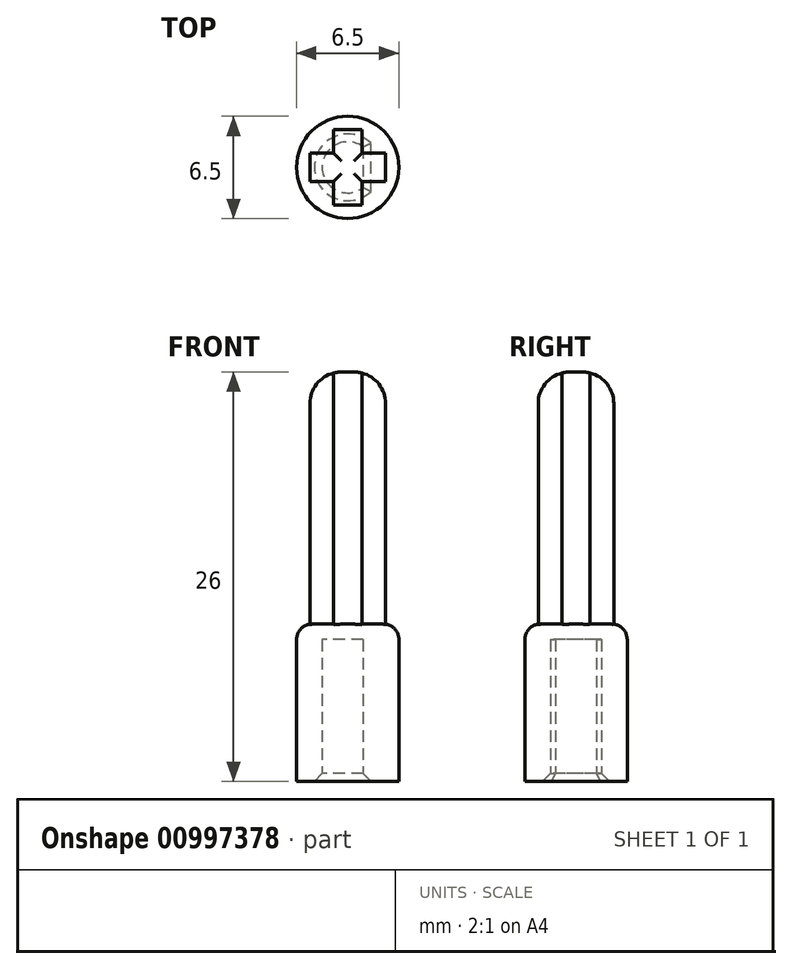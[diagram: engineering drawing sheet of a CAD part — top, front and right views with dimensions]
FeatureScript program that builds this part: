
annotation { "Feature Type Name" : "Feature", "Feature Type Description" : "" }
export const myFeature = defineFeature(function(context is Context, id is Id, definition is map)
    precondition{}
    {
        {
            var Q0;
            Q0=qCreatedBy(makeId("Top.planeOp"),FACE);
            var sketch = newSketch(context, id + "F0", { "sketchPlane" : qUnion([Q0])});
            skCircle(sketch, "E0", {"center": v(0, 0) * mm, "radius": 3.25 * mm});
            skCircle(sketch, "E1", {"center": v(0, 0) * mm, "radius": 1.63 * mm});
            skLineSegment(sketch, "E2", {"start": v(0.98, 1.3) * mm, "end": v(0.98, -1.3) * mm});
            skSolve(sketch);
        }
        {
            var Q0;
            Q0=makeQuery(id+"F0.imprint","IMPRINT",FACE,{"disambiguationData":[TD([[makeQuery(id+"F0.imprint","IMPRINT",EDGE,{"derivedFrom":sQuery(id+"F0.wireOp",EDGE,"E0")}),1.0]])]});
            var Q1;
            {var subQ0=sQuery(id+"F0.wireOp",EDGE,"E2");Q1=makeQuery(id+"F0.imprint","IMPRINT",FACE,{"disambiguationData":[TD([[makeQuery(id+"F0.imprint","IMPRINT",EDGE,{"derivedFrom":subQ0}),1.0]])]});}
            extrude(context, id + "F1", {"entities" : qUnion([Q0, Q1]), "depth" : 9 * mm, "offsetDistance" : 25 * mm});
        }
        {
            var Q0;
            Q0=makeQuery(id+"F1.opExtrude","CAP_FACE",FACE,{"disambiguationData":[OSD([sQuery(id+"F0.wireOp",EDGE,"E0"),sQuery(id+"F0.wireOp",EDGE,"E1"),sQuery(id+"F0.wireOp",EDGE,"E2")])],"isStart":false});
            var sketch = newSketch(context, id + "F2", { "sketchPlane" : qUnion([Q0])});
            skCircle(sketch, "E3", {"center": v(0, 0) * mm, "radius": 3.25 * mm});
            skSolve(sketch);
        }
        {
            var Q0;
            Q0 = qSketchRegion(id + "F2", true);
            extrude(context, id + "F3", {"entities" : qUnion([Q0]), "operationType" : NewBodyOperationType.ADD, "depth" : 1 * mm, "offsetDistance" : 25 * mm});
        }
        {
            var Q0;
            Q0=makeQuery(id+"F3.opExtrude","CAP_FACE",FACE,{"disambiguationData":[OSD([sQuery(id+"F2.wireOp",EDGE,"E3")])],"isStart":false});
            var sketch = newSketch(context, id + "F4", { "sketchPlane" : qUnion([Q0])});
            skLineSegment(sketch, "E4", {"start": v(-2.4, 0.9) * mm, "end": v(-2.4, -0.9) * mm});
            skLineSegment(sketch, "E5", {"start": v(-2.4, -0.9) * mm, "end": v(-0.9, -0.9) * mm});
            skLineSegment(sketch, "E6", {"start": v(-0.9, -0.9) * mm, "end": v(-0.9, -2.4) * mm});
            skLineSegment(sketch, "E7", {"start": v(-0.9, -2.4) * mm, "end": v(0.9, -2.4) * mm});
            skLineSegment(sketch, "E8", {"start": v(0.9, -2.4) * mm, "end": v(0.9, -0.9) * mm});
            skLineSegment(sketch, "E9", {"start": v(0.9, -0.9) * mm, "end": v(2.4, -0.9) * mm});
            skLineSegment(sketch, "E10", {"start": v(2.4, -0.9) * mm, "end": v(2.4, 0.9) * mm});
            skLineSegment(sketch, "E11", {"start": v(2.4, 0.9) * mm, "end": v(0.9, 0.9) * mm});
            skLineSegment(sketch, "E12", {"start": v(0.9, 0.9) * mm, "end": v(0.9, 2.4) * mm});
            skLineSegment(sketch, "E13", {"start": v(0.9, 2.4) * mm, "end": v(-0.9, 2.4) * mm});
            skLineSegment(sketch, "E14", {"start": v(-0.9, 2.4) * mm, "end": v(-0.9, 0.9) * mm});
            skLineSegment(sketch, "E15", {"start": v(-0.9, 0.9) * mm, "end": v(-2.4, 0.9) * mm});
            skSolve(sketch);
        }
        {
            var Q0;
            Q0=makeQuery(id+"F4.imprint","IMPRINT",FACE,{"disambiguationData":[TD([[makeQuery(id+"F4.imprint","IMPRINT",EDGE,{"derivedFrom":sQuery(id+"F4.wireOp",EDGE,"E4")}),1.0]])]});
            extrude(context, id + "F5", {"entities" : qUnion([Q0]), "operationType" : NewBodyOperationType.ADD, "depth" : 16 * mm, "offsetDistance" : 25 * mm});
        }
        {
            var Q0;
            Q0=makeQuery(id+"F5.opExtrude","CAP_EDGE",EDGE,{"disambiguationData":[OSD([sQuery(id+"F4.wireOp",EDGE,"E7")])],"isStart":false});
            var Q1;
            Q1=makeQuery(id+"F5.opExtrude","CAP_EDGE",EDGE,{"disambiguationData":[OSD([sQuery(id+"F4.wireOp",EDGE,"E10")])],"isStart":false});
            var Q2;
            Q2=makeQuery(id+"F5.opExtrude","CAP_EDGE",EDGE,{"disambiguationData":[OSD([sQuery(id+"F4.wireOp",EDGE,"E13")])],"isStart":false});
            var Q3;
            Q3=makeQuery(id+"F5.opExtrude","CAP_EDGE",EDGE,{"disambiguationData":[OSD([sQuery(id+"F4.wireOp",EDGE,"E4")])],"isStart":false});
            fillet(context, id + "F6", {"entities" : qUnion([Q0, Q1, Q2, Q3]), "radius" : 2 * mm, "tangentPropagation" : true, "allowEdgeOverflow" : false});
        }
        {
            var Q0;
            Q0=makeQuery(id+"F3.opExtrude","CAP_EDGE",EDGE,{"disambiguationData":[OSD([sQuery(id+"F2.wireOp",EDGE,"E3")])],"isStart":false});
            fillet(context, id + "F7", {"entities" : qUnion([Q0]), "radius" : 1 * mm, "tangentPropagation" : true, "allowEdgeOverflow" : false});
        }
        {
            var Q0;
            Q0=makeQuery(id+"F1.opExtrude","CAP_EDGE",EDGE,{"disambiguationData":[OSD([sQuery(id+"F0.wireOp",EDGE,"E1")])],"isStart":true});
            var Q1;
            Q1=makeQuery(id+"F1.opExtrude","CAP_EDGE",EDGE,{"disambiguationData":[OSD([sQuery(id+"F0.wireOp",EDGE,"E2")])],"isStart":true});
            chamfer(context, id + "F8", {"entities" : qUnion([Q0, Q1]), "width" : .5 * mm, "tangentPropagation" : true});
        }
    });
